# Revit family: Andreu World_Raglan_SF2066
name_source: partatom
category: Mobiliario
revit_build: Autodesk Revit 2013 (Build: 20120221_2030(x64)
units: mm (PartAtom-declared; Revit-internal decimal feet)

## types (1)
- Andreu World_Raglan_SF-2066
    Base Material = Andreu World Polished Aluminum
    Depth = 750 mm  [stored 2.46063 ft]
    Descripción = 2-seater sofa with upholstered seat and backrest and 4-legged aluminum injected base.
    Fabricante = Andreu World
    Height = 720 mm  [stored 2.3622 ft]
    Legs Height = 240 mm  [stored 0.787402 ft]
    Modelo = Raglan
    Piping Material = Andreu World Leather, Black
    Reference = BU-2066
    Seat Height = 860 mm  [stored 2.82152 ft]
    Seat Material = Andreu World Fabric
    URL = http://www.andreuworld.com
    Width = 1600 mm  [stored 5.24934 ft]

note: [stored X ft] marks values corroborated as IEEE doubles in the binary element streams (Revit-internal decimal feet)

## geometry (parser evidence)
native form markers: Blend x14, Sweep x1
no freeform markers — native parametric forms only
